# Revit family: FK038-16 x16 x X
name_source: partatom
category: Furniture
units: mm (PartAtom-declared; Revit-internal decimal feet)

## family parameters
Always vertical = Yes
Cut with Voids When Loaded = No
OmniClass Number = 23.40.20.00
OmniClass Title = General Furniture and Specialties
Room Calculation Point = No
Shared = No
Work Plane-Based = No

## types (2) — shared parameters
Low Emitting Finish = Yes
Low Emitting Material = Yes
Manufacturer = Fomcore
Salvage or Reuse = Yes
Seat = <By Category>
Side = <By Category>
Type Comments = Square Lily Pad
URL = https://fomcore.com
zero-valued in all types: Cost, Percentage of Recycled Content

## per-type parameters (varying)
| type | Description | H |
| FK038-16x16x6-Z | 6" Square Lily Pad, 16"Lx16"Wx6"H, Zippered (Minimum Order of 5 Quantity) | 6" |
| FK038-16x16x3-Z | 3" Square Lily Pad, 16"Lx16"Wx3"H, Zippered (Minimum Order of 10 Quantity) | 3" |

note: column(s) folded — value = type name in every type: Model

## geometry (parser evidence)
native form markers: Sweep x2
no freeform markers — native parametric forms only
